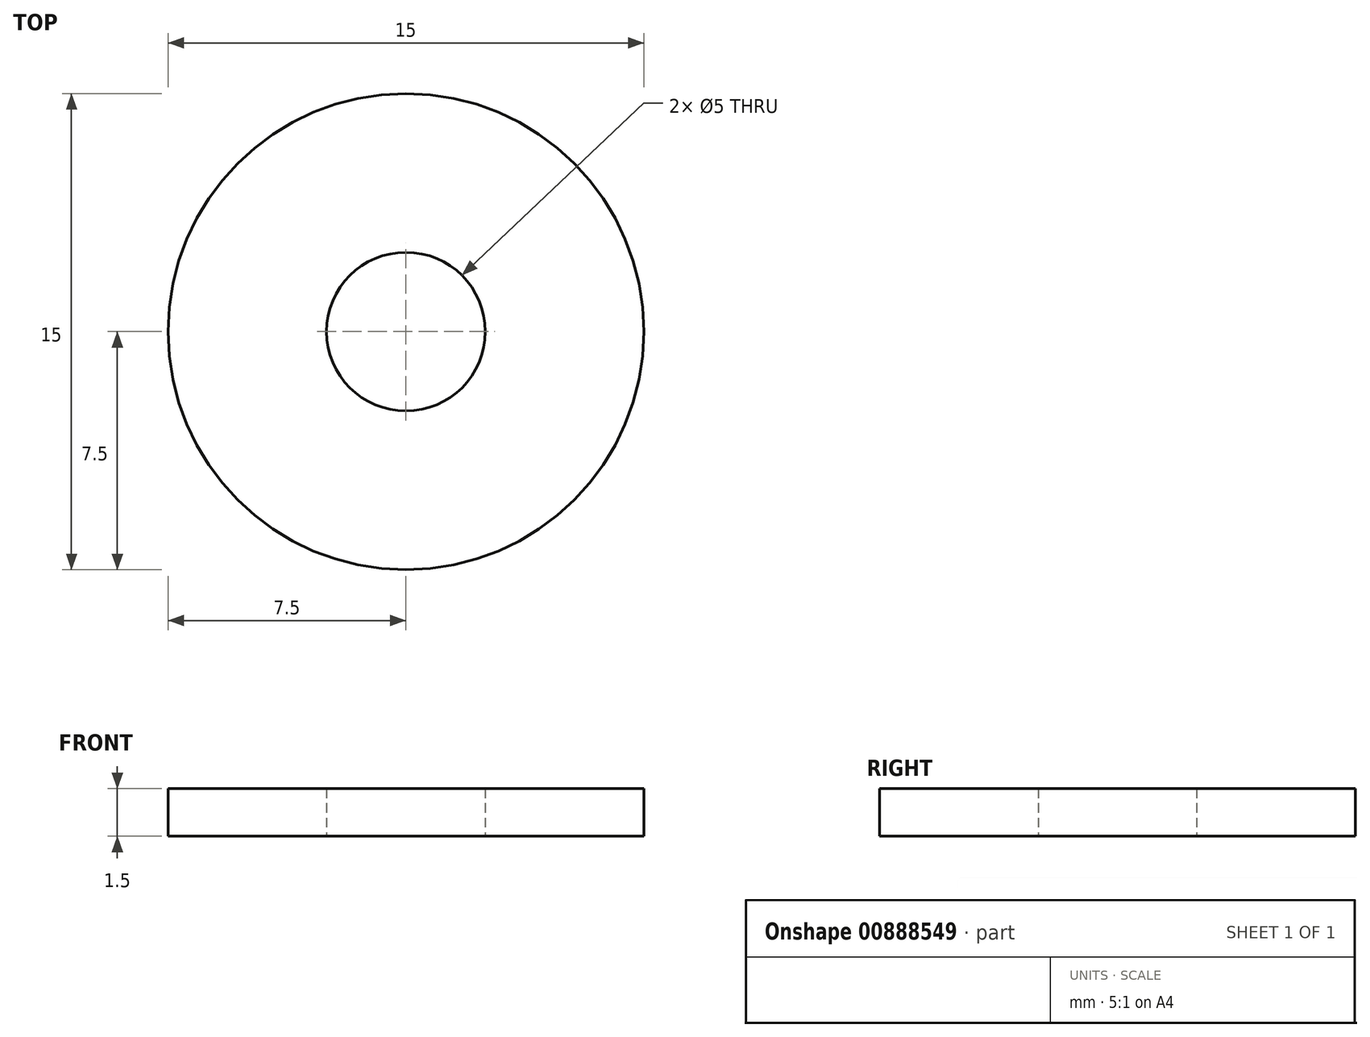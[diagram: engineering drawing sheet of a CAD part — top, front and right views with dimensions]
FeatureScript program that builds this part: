
annotation { "Feature Type Name" : "Feature", "Feature Type Description" : "" }
export const myFeature = defineFeature(function(context is Context, id is Id, definition is map)
    precondition{}
    {
        {
            var Q0;
            Q0=qCreatedBy(makeId("Top.planeOp"),FACE);
            var sketch = newSketch(context, id + "F0", { "sketchPlane" : qUnion([Q0])});
            skCircle(sketch, "E0", {"center": v(0, 0) * mm, "radius": 2.5 * mm});
            skCircle(sketch, "E1", {"center": v(0, 0) * mm, "radius": 7.5 * mm});
            skSolve(sketch);
        }
        {
            var Q0;
            Q0 = qSketchRegion(id + "F0", true);
            extrude(context, id + "F1", {"entities" : qUnion([Q0]), "depth" : 1.5 * mm, "offsetDistance" : 25 * mm});
        }
    });
